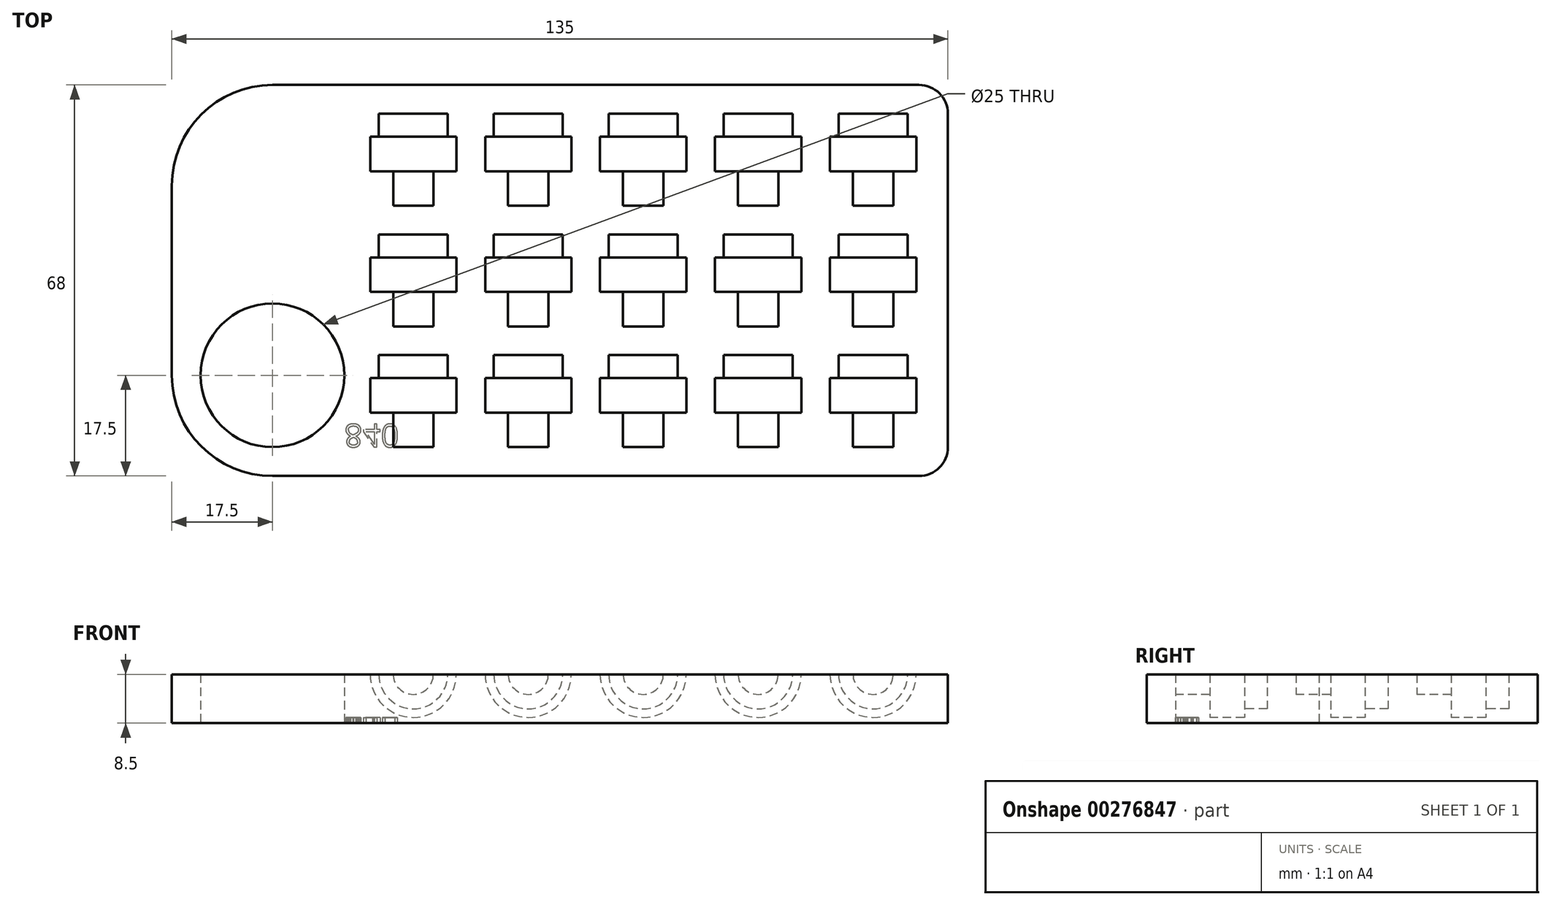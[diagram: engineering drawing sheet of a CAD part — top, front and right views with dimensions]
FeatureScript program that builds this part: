
annotation { "Feature Type Name" : "Feature", "Feature Type Description" : "" }
export const myFeature = defineFeature(function(context is Context, id is Id, definition is map)
    precondition{}
    {
        {
            var Q0;
            Q0=qCreatedBy(makeId("Top.planeOp"),FACE);
            var sketch = newSketch(context, id + "F0", { "sketchPlane" : qUnion([Q0])});
            skLineSegment(sketch, "E0.bottom", {"start": v(17.5, 0) * mm, "end": v(130, 0) * mm});
            skLineSegment(sketch, "E0.top", {"start": v(17.5, 68) * mm, "end": v(130, 68) * mm});
            skLineSegment(sketch, "E0.left", {"start": v(0, 17.5) * mm, "end": v(0, 50.5) * mm});
            skLineSegment(sketch, "E0.right", {"start": v(135, 5) * mm, "end": v(135, 63) * mm});
            skLineSegment(sketch, "E1.bottom", {"start": v(0, 0) * mm, "end": v(17.5, 0) * mm, "construction": true});
            skLineSegment(sketch, "E1.top", {"start": v(0, 17.5) * mm, "end": v(17.5, 17.5) * mm, "construction": true});
            skLineSegment(sketch, "E1.left", {"start": v(0, 0) * mm, "end": v(0, 17.5) * mm, "construction": true});
            skLineSegment(sketch, "E1.right", {"start": v(17.5, 0) * mm, "end": v(17.5, 17.5) * mm, "construction": true});
            skCircle(sketch, "E2", {"center": v(17.5, 17.5) * mm, "radius": 12.5 * mm});
            skPoint(sketch, "E3.visualSharp", {"position": v(0, 0) * mm});
            skArc(sketch, "E3.filletArc", {"start": v(0, 17.5) * mm, "mid": v(5.13, 5.13) * mm, "end": v(17.5, 0) * mm});
            skPoint(sketch, "E4.visualSharp", {"position": v(0, 68) * mm});
            skArc(sketch, "E4.filletArc", {"start": v(17.5, 68) * mm, "mid": v(5.13, 62.87) * mm, "end": v(0, 50.5) * mm});
            skPoint(sketch, "E5.visualSharp", {"position": v(135, 68) * mm});
            skArc(sketch, "E5.filletArc", {"start": v(135, 63) * mm, "mid": v(133.54, 66.54) * mm, "end": v(130, 68) * mm});
            skPoint(sketch, "E6.visualSharp", {"position": v(135, 0) * mm});
            skArc(sketch, "E6.filletArc", {"start": v(130, 0) * mm, "mid": v(133.54, 1.46) * mm, "end": v(135, 5) * mm});
            skSolve(sketch);
        }
        {
            var Q0;
            Q0=makeQuery(id+"F0.imprint","IMPRINT",FACE,{"disambiguationData":[TD([[makeQuery(id+"F0.imprint","IMPRINT",EDGE,{"derivedFrom":sQuery(id+"F0.wireOp",EDGE,"E0.bottom")}),1.0]])]});
            extrude(context, id + "F1", {"entities" : qUnion([Q0]), "depth" : 8.5 * mm});
        }
        {
            var Q0;
            Q0=makeQuery(id+"F1.opExtrude","CAP_FACE",FACE,{"disambiguationData":[OSD([sQuery(id+"F0.wireOp",EDGE,"E0.bottom"),sQuery(id+"F0.wireOp",EDGE,"E0.top"),sQuery(id+"F0.wireOp",EDGE,"E0.left"),sQuery(id+"F0.wireOp",EDGE,"E0.right"),sQuery(id+"F0.wireOp",EDGE,"E2"),sQuery(id+"F0.wireOp",EDGE,"E3.filletArc"),sQuery(id+"F0.wireOp",EDGE,"E4.filletArc"),sQuery(id+"F0.wireOp",EDGE,"E5.filletArc"),sQuery(id+"F0.wireOp",EDGE,"E6.filletArc")])],"isStart":false});
            var sketch = newSketch(context, id + "F2", { "sketchPlane" : qUnion([Q0])});
            skLineSegment(sketch, "E7.bottom", {"start": v(0, 0) * mm, "end": v(42, 0) * mm, "construction": true});
            skLineSegment(sketch, "E7.top", {"start": v(0, 21) * mm, "end": v(42, 21) * mm, "construction": true});
            skLineSegment(sketch, "E7.left", {"start": v(0, 0) * mm, "end": v(0, 21) * mm, "construction": true});
            skLineSegment(sketch, "E7.right", {"start": v(42, 0) * mm, "end": v(42, 21) * mm, "construction": true});
            skLineSegment(sketch, "E8.bottom", {"start": v(42, 21) * mm, "end": v(62, 21) * mm, "construction": true});
            skLineSegment(sketch, "E8.top", {"start": v(42, 42) * mm, "end": v(62, 42) * mm, "construction": true});
            skLineSegment(sketch, "E8.left", {"start": v(42, 21) * mm, "end": v(42, 42) * mm, "construction": true});
            skLineSegment(sketch, "E8.right", {"start": v(62, 21) * mm, "end": v(62, 42) * mm, "construction": true});
            skLineSegment(sketch, "E9.top", {"start": v(42, 63) * mm, "end": v(62, 63) * mm, "construction": true});
            skLineSegment(sketch, "E9.left", {"start": v(42, 42) * mm, "end": v(42, 63) * mm, "construction": true});
            skLineSegment(sketch, "E9.right", {"start": v(62, 42) * mm, "end": v(62, 63) * mm, "construction": true});
            skLineSegment(sketch, "E10.bottom", {"start": v(62, 21) * mm, "end": v(82, 21) * mm, "construction": true});
            skLineSegment(sketch, "E10.top", {"start": v(62, 42) * mm, "end": v(82, 42) * mm, "construction": true});
            skLineSegment(sketch, "E10.right", {"start": v(82, 21) * mm, "end": v(82, 42) * mm, "construction": true});
            skLineSegment(sketch, "E11.top", {"start": v(62, 63) * mm, "end": v(82, 63) * mm, "construction": true});
            skLineSegment(sketch, "E11.right", {"start": v(82, 42) * mm, "end": v(82, 63) * mm, "construction": true});
            skLineSegment(sketch, "E12.bottom", {"start": v(82, 21) * mm, "end": v(102, 21) * mm, "construction": true});
            skLineSegment(sketch, "E12.top", {"start": v(82, 42) * mm, "end": v(102, 42) * mm, "construction": true});
            skLineSegment(sketch, "E12.right", {"start": v(102, 21) * mm, "end": v(102, 42) * mm, "construction": true});
            skLineSegment(sketch, "E13.top", {"start": v(82, 63) * mm, "end": v(102, 63) * mm, "construction": true});
            skLineSegment(sketch, "E13.right", {"start": v(102, 42) * mm, "end": v(102, 63) * mm, "construction": true});
            skLineSegment(sketch, "E14.bottom", {"start": v(102, 21) * mm, "end": v(122, 21) * mm, "construction": true});
            skLineSegment(sketch, "E14.top", {"start": v(102, 42) * mm, "end": v(122, 42) * mm, "construction": true});
            skLineSegment(sketch, "E14.right", {"start": v(122, 21) * mm, "end": v(122, 42) * mm, "construction": true});
            skLineSegment(sketch, "E15.top", {"start": v(102, 63) * mm, "end": v(122, 63) * mm, "construction": true});
            skLineSegment(sketch, "E15.right", {"start": v(122, 42) * mm, "end": v(122, 63) * mm, "construction": true});
            skLineSegment(sketch, "E16.bottom", {"start": v(42, 63) * mm, "end": v(48, 63) * mm});
            skLineSegment(sketch, "E16.left", {"start": v(42, 63) * mm, "end": v(42, 59) * mm});
            skLineSegment(sketch, "E16.right", {"start": v(48, 63) * mm, "end": v(48, 59) * mm});
            skLineSegment(sketch, "E17.bottom", {"start": v(62, 63) * mm, "end": v(68, 63) * mm});
            skLineSegment(sketch, "E17.left", {"start": v(62, 63) * mm, "end": v(62, 59) * mm});
            skLineSegment(sketch, "E17.right", {"start": v(68, 63) * mm, "end": v(68, 59) * mm});
            skLineSegment(sketch, "E18.bottom", {"start": v(82, 63) * mm, "end": v(88, 63) * mm});
            skLineSegment(sketch, "E18.left", {"start": v(82, 63) * mm, "end": v(82, 59) * mm});
            skLineSegment(sketch, "E18.right", {"start": v(88, 63) * mm, "end": v(88, 59) * mm});
            skLineSegment(sketch, "E19.bottom", {"start": v(102, 63) * mm, "end": v(108, 63) * mm});
            skLineSegment(sketch, "E19.left", {"start": v(102, 63) * mm, "end": v(102, 59) * mm});
            skLineSegment(sketch, "E19.right", {"start": v(108, 63) * mm, "end": v(108, 59) * mm});
            skLineSegment(sketch, "E20.bottom", {"start": v(42, 42) * mm, "end": v(48, 42) * mm});
            skLineSegment(sketch, "E20.left", {"start": v(42, 42) * mm, "end": v(42, 38) * mm});
            skLineSegment(sketch, "E20.right", {"start": v(48, 42) * mm, "end": v(48, 38) * mm});
            skLineSegment(sketch, "E21.bottom", {"start": v(62, 42) * mm, "end": v(68, 42) * mm});
            skLineSegment(sketch, "E21.left", {"start": v(62, 42) * mm, "end": v(62, 38) * mm});
            skLineSegment(sketch, "E21.right", {"start": v(68, 42) * mm, "end": v(68, 38) * mm});
            skLineSegment(sketch, "E22.bottom", {"start": v(82, 42) * mm, "end": v(88, 42) * mm});
            skLineSegment(sketch, "E22.left", {"start": v(82, 42) * mm, "end": v(82, 38) * mm});
            skLineSegment(sketch, "E22.right", {"start": v(88, 42) * mm, "end": v(88, 38) * mm});
            skLineSegment(sketch, "E23.bottom", {"start": v(102, 42) * mm, "end": v(108, 42) * mm});
            skLineSegment(sketch, "E23.left", {"start": v(102, 42) * mm, "end": v(102, 38) * mm});
            skLineSegment(sketch, "E23.right", {"start": v(108, 42) * mm, "end": v(108, 38) * mm});
            skLineSegment(sketch, "E24.bottom", {"start": v(42, 21) * mm, "end": v(48, 21) * mm});
            skLineSegment(sketch, "E24.left", {"start": v(42, 21) * mm, "end": v(42, 17) * mm});
            skLineSegment(sketch, "E24.right", {"start": v(48, 21) * mm, "end": v(48, 17) * mm});
            skPoint(sketch, "E25.oppositeSnap0", {"position": v(68, 40) * mm});
            skLineSegment(sketch, "E25.bottom", {"start": v(62, 21) * mm, "end": v(68, 21) * mm});
            skLineSegment(sketch, "E25.left", {"start": v(62, 21) * mm, "end": v(62, 17) * mm});
            skLineSegment(sketch, "E25.right", {"start": v(68, 21) * mm, "end": v(68, 17) * mm});
            skLineSegment(sketch, "E26.bottom", {"start": v(82, 21) * mm, "end": v(88, 21) * mm});
            skLineSegment(sketch, "E26.left", {"start": v(82, 21) * mm, "end": v(82, 17) * mm});
            skLineSegment(sketch, "E26.right", {"start": v(88, 21) * mm, "end": v(88, 17) * mm});
            skLineSegment(sketch, "E27.bottom", {"start": v(102, 21) * mm, "end": v(108, 21) * mm});
            skLineSegment(sketch, "E27.left", {"start": v(102, 21) * mm, "end": v(102, 17) * mm});
            skLineSegment(sketch, "E27.right", {"start": v(108, 21) * mm, "end": v(108, 17) * mm});
            skLineSegment(sketch, "E28.bottom", {"start": v(48, 59) * mm, "end": v(49.5, 59) * mm});
            skLineSegment(sketch, "E28.top", {"start": v(45.5, 53) * mm, "end": v(49.5, 53) * mm});
            skLineSegment(sketch, "E28.left", {"start": v(42, 59) * mm, "end": v(42, 53) * mm});
            skLineSegment(sketch, "E28.right", {"start": v(49.5, 59) * mm, "end": v(49.5, 53) * mm});
            skLineSegment(sketch, "E29.bottom", {"start": v(68, 59) * mm, "end": v(69.5, 59) * mm});
            skLineSegment(sketch, "E29.top", {"start": v(65.5, 53) * mm, "end": v(69.5, 53) * mm});
            skLineSegment(sketch, "E29.left", {"start": v(62, 59) * mm, "end": v(62, 53) * mm});
            skLineSegment(sketch, "E29.right", {"start": v(69.5, 59) * mm, "end": v(69.5, 53) * mm});
            skLineSegment(sketch, "E30.bottom", {"start": v(88, 59) * mm, "end": v(89.5, 59) * mm});
            skLineSegment(sketch, "E30.top", {"start": v(85.5, 53) * mm, "end": v(89.5, 53) * mm});
            skLineSegment(sketch, "E30.left", {"start": v(82, 59) * mm, "end": v(82, 53) * mm});
            skLineSegment(sketch, "E30.right", {"start": v(89.5, 59) * mm, "end": v(89.5, 53) * mm});
            skLineSegment(sketch, "E31.bottom", {"start": v(108, 59) * mm, "end": v(109.5, 59) * mm});
            skLineSegment(sketch, "E31.top", {"start": v(105.5, 53) * mm, "end": v(109.5, 53) * mm});
            skLineSegment(sketch, "E31.left", {"start": v(102, 59) * mm, "end": v(102, 53) * mm});
            skLineSegment(sketch, "E31.right", {"start": v(109.5, 59) * mm, "end": v(109.5, 53) * mm});
            skLineSegment(sketch, "E32.bottom", {"start": v(48, 38) * mm, "end": v(49.5, 38) * mm});
            skLineSegment(sketch, "E32.top", {"start": v(45.5, 32) * mm, "end": v(49.5, 32) * mm});
            skLineSegment(sketch, "E32.left", {"start": v(42, 38) * mm, "end": v(42, 32) * mm});
            skLineSegment(sketch, "E32.right", {"start": v(49.5, 38) * mm, "end": v(49.5, 32) * mm});
            skLineSegment(sketch, "E33.bottom", {"start": v(68, 38) * mm, "end": v(69.5, 38) * mm});
            skLineSegment(sketch, "E33.top", {"start": v(65.5, 32) * mm, "end": v(69.5, 32) * mm});
            skLineSegment(sketch, "E33.left", {"start": v(62, 38) * mm, "end": v(62, 32) * mm});
            skLineSegment(sketch, "E33.right", {"start": v(69.5, 38) * mm, "end": v(69.5, 32) * mm});
            skLineSegment(sketch, "E34.bottom", {"start": v(88, 38) * mm, "end": v(89.5, 38) * mm});
            skLineSegment(sketch, "E34.top", {"start": v(85.5, 32) * mm, "end": v(89.5, 32) * mm});
            skLineSegment(sketch, "E34.left", {"start": v(82, 38) * mm, "end": v(82, 32) * mm});
            skLineSegment(sketch, "E34.right", {"start": v(89.5, 38) * mm, "end": v(89.5, 32) * mm});
            skLineSegment(sketch, "E35.bottom", {"start": v(108, 38) * mm, "end": v(109.5, 38) * mm});
            skLineSegment(sketch, "E35.top", {"start": v(105.5, 32) * mm, "end": v(109.5, 32) * mm});
            skLineSegment(sketch, "E35.left", {"start": v(102, 38) * mm, "end": v(102, 32) * mm});
            skLineSegment(sketch, "E35.right", {"start": v(109.5, 38) * mm, "end": v(109.5, 32) * mm});
            skLineSegment(sketch, "E36.bottom", {"start": v(48, 17) * mm, "end": v(49.5, 17) * mm});
            skLineSegment(sketch, "E36.top", {"start": v(45.5, 11) * mm, "end": v(49.5, 11) * mm});
            skLineSegment(sketch, "E36.left", {"start": v(42, 17) * mm, "end": v(42, 11) * mm});
            skLineSegment(sketch, "E36.right", {"start": v(49.5, 17) * mm, "end": v(49.5, 11) * mm});
            skLineSegment(sketch, "E37.bottom", {"start": v(68, 17) * mm, "end": v(69.5, 17) * mm});
            skLineSegment(sketch, "E37.top", {"start": v(65.5, 11) * mm, "end": v(69.5, 11) * mm});
            skLineSegment(sketch, "E37.left", {"start": v(62, 17) * mm, "end": v(62, 11) * mm});
            skLineSegment(sketch, "E37.right", {"start": v(69.5, 17) * mm, "end": v(69.5, 11) * mm});
            skLineSegment(sketch, "E38.bottom", {"start": v(88, 17) * mm, "end": v(89.5, 17) * mm});
            skLineSegment(sketch, "E38.top", {"start": v(85.5, 11) * mm, "end": v(89.5, 11) * mm});
            skLineSegment(sketch, "E38.left", {"start": v(82, 17) * mm, "end": v(82, 11) * mm});
            skLineSegment(sketch, "E38.right", {"start": v(89.5, 17) * mm, "end": v(89.5, 11) * mm});
            skLineSegment(sketch, "E39.bottom", {"start": v(108, 17) * mm, "end": v(109.5, 17) * mm});
            skLineSegment(sketch, "E39.top", {"start": v(105.5, 11) * mm, "end": v(109.5, 11) * mm});
            skLineSegment(sketch, "E39.left", {"start": v(102, 17) * mm, "end": v(102, 11) * mm});
            skLineSegment(sketch, "E39.right", {"start": v(109.5, 17) * mm, "end": v(109.5, 11) * mm});
            skLineSegment(sketch, "E40.top", {"start": v(42, 47) * mm, "end": v(45.5, 47) * mm});
            skLineSegment(sketch, "E40.left", {"start": v(42, 53) * mm, "end": v(42, 47) * mm});
            skLineSegment(sketch, "E40.right", {"start": v(45.5, 53) * mm, "end": v(45.5, 47) * mm});
            skLineSegment(sketch, "E41.top", {"start": v(62, 47) * mm, "end": v(65.5, 47) * mm});
            skLineSegment(sketch, "E41.left", {"start": v(62, 53) * mm, "end": v(62, 47) * mm});
            skLineSegment(sketch, "E41.right", {"start": v(65.5, 53) * mm, "end": v(65.5, 47) * mm});
            skLineSegment(sketch, "E42.top", {"start": v(82, 47) * mm, "end": v(85.5, 47) * mm});
            skLineSegment(sketch, "E42.left", {"start": v(82, 53) * mm, "end": v(82, 47) * mm});
            skLineSegment(sketch, "E42.right", {"start": v(85.5, 53) * mm, "end": v(85.5, 47) * mm});
            skLineSegment(sketch, "E43.top", {"start": v(102, 47) * mm, "end": v(105.5, 47) * mm});
            skLineSegment(sketch, "E43.left", {"start": v(102, 53) * mm, "end": v(102, 47) * mm});
            skLineSegment(sketch, "E43.right", {"start": v(105.5, 53) * mm, "end": v(105.5, 47) * mm});
            skLineSegment(sketch, "E44.top", {"start": v(42, 26) * mm, "end": v(45.5, 26) * mm});
            skLineSegment(sketch, "E44.left", {"start": v(42, 32) * mm, "end": v(42, 26) * mm});
            skLineSegment(sketch, "E44.right", {"start": v(45.5, 32) * mm, "end": v(45.5, 26) * mm});
            skLineSegment(sketch, "E45.top", {"start": v(62, 26) * mm, "end": v(65.5, 26) * mm});
            skLineSegment(sketch, "E45.left", {"start": v(62, 32) * mm, "end": v(62, 26) * mm});
            skLineSegment(sketch, "E45.right", {"start": v(65.5, 32) * mm, "end": v(65.5, 26) * mm});
            skLineSegment(sketch, "E46.top", {"start": v(82, 26) * mm, "end": v(85.5, 26) * mm});
            skLineSegment(sketch, "E46.left", {"start": v(82, 32) * mm, "end": v(82, 26) * mm});
            skLineSegment(sketch, "E46.right", {"start": v(85.5, 32) * mm, "end": v(85.5, 26) * mm});
            skLineSegment(sketch, "E47.top", {"start": v(102, 26) * mm, "end": v(105.5, 26) * mm});
            skLineSegment(sketch, "E47.left", {"start": v(102, 32) * mm, "end": v(102, 26) * mm});
            skLineSegment(sketch, "E47.right", {"start": v(105.5, 32) * mm, "end": v(105.5, 26) * mm});
            skLineSegment(sketch, "E48.top", {"start": v(42, 5) * mm, "end": v(45.5, 5) * mm});
            skLineSegment(sketch, "E48.left", {"start": v(42, 11) * mm, "end": v(42, 5) * mm});
            skLineSegment(sketch, "E48.right", {"start": v(45.5, 11) * mm, "end": v(45.5, 5) * mm});
            skPoint(sketch, "E49.oppositeSnap0", {"position": v(43.75, 5) * mm});
            skLineSegment(sketch, "E49.top", {"start": v(62, 5) * mm, "end": v(65.5, 5) * mm});
            skLineSegment(sketch, "E49.left", {"start": v(62, 11) * mm, "end": v(62, 5) * mm});
            skLineSegment(sketch, "E49.right", {"start": v(65.5, 11) * mm, "end": v(65.5, 5) * mm});
            skLineSegment(sketch, "E50.top", {"start": v(82, 5) * mm, "end": v(85.5, 5) * mm});
            skLineSegment(sketch, "E50.left", {"start": v(82, 11) * mm, "end": v(82, 5) * mm});
            skLineSegment(sketch, "E50.right", {"start": v(85.5, 11) * mm, "end": v(85.5, 5) * mm});
            skLineSegment(sketch, "E51.top", {"start": v(102, 5) * mm, "end": v(105.5, 5) * mm});
            skLineSegment(sketch, "E51.left", {"start": v(102, 11) * mm, "end": v(102, 5) * mm});
            skLineSegment(sketch, "E51.right", {"start": v(105.5, 11) * mm, "end": v(105.5, 5) * mm});
            skLineSegment(sketch, "E52.bottom", {"start": v(122, 63) * mm, "end": v(128, 63) * mm});
            skLineSegment(sketch, "E52.left", {"start": v(122, 63) * mm, "end": v(122, 59) * mm});
            skLineSegment(sketch, "E52.right", {"start": v(128, 63) * mm, "end": v(128, 59) * mm});
            skLineSegment(sketch, "E53.bottom", {"start": v(122, 42) * mm, "end": v(128, 42) * mm});
            skLineSegment(sketch, "E53.left", {"start": v(122, 42) * mm, "end": v(122, 38) * mm});
            skLineSegment(sketch, "E53.right", {"start": v(128, 42) * mm, "end": v(128, 38) * mm});
            skLineSegment(sketch, "E54.bottom", {"start": v(122, 21) * mm, "end": v(128, 21) * mm});
            skLineSegment(sketch, "E54.left", {"start": v(122, 21) * mm, "end": v(122, 17) * mm});
            skLineSegment(sketch, "E54.right", {"start": v(128, 21) * mm, "end": v(128, 17) * mm});
            skLineSegment(sketch, "E55.bottom", {"start": v(128, 59) * mm, "end": v(129.5, 59) * mm});
            skLineSegment(sketch, "E55.top", {"start": v(125.5, 53) * mm, "end": v(129.5, 53) * mm});
            skLineSegment(sketch, "E55.left", {"start": v(122, 59) * mm, "end": v(122, 53) * mm});
            skLineSegment(sketch, "E55.right", {"start": v(129.5, 59) * mm, "end": v(129.5, 53) * mm});
            skLineSegment(sketch, "E56.bottom", {"start": v(128, 38) * mm, "end": v(129.5, 38) * mm});
            skLineSegment(sketch, "E56.top", {"start": v(125.5, 32) * mm, "end": v(129.5, 32) * mm});
            skLineSegment(sketch, "E56.left", {"start": v(122, 38) * mm, "end": v(122, 32) * mm});
            skLineSegment(sketch, "E56.right", {"start": v(129.5, 38) * mm, "end": v(129.5, 32) * mm});
            skLineSegment(sketch, "E57.bottom", {"start": v(128, 17) * mm, "end": v(129.5, 17) * mm});
            skLineSegment(sketch, "E57.top", {"start": v(125.5, 11) * mm, "end": v(129.5, 11) * mm});
            skLineSegment(sketch, "E57.left", {"start": v(122, 17) * mm, "end": v(122, 11) * mm});
            skLineSegment(sketch, "E57.right", {"start": v(129.5, 17) * mm, "end": v(129.5, 11) * mm});
            skLineSegment(sketch, "E58.top", {"start": v(122, 47) * mm, "end": v(125.5, 47) * mm});
            skLineSegment(sketch, "E58.left", {"start": v(122, 53) * mm, "end": v(122, 47) * mm});
            skLineSegment(sketch, "E58.right", {"start": v(125.5, 53) * mm, "end": v(125.5, 47) * mm});
            skLineSegment(sketch, "E59.top", {"start": v(122, 26) * mm, "end": v(125.5, 26) * mm});
            skLineSegment(sketch, "E59.left", {"start": v(122, 32) * mm, "end": v(122, 26) * mm});
            skLineSegment(sketch, "E59.right", {"start": v(125.5, 32) * mm, "end": v(125.5, 26) * mm});
            skLineSegment(sketch, "E60.top", {"start": v(122, 5) * mm, "end": v(125.5, 5) * mm});
            skLineSegment(sketch, "E60.left", {"start": v(122, 11) * mm, "end": v(122, 5) * mm});
            skLineSegment(sketch, "E60.right", {"start": v(125.5, 11) * mm, "end": v(125.5, 5) * mm});
            skSolve(sketch);
        }
        {
            var Q0;
            Q0=makeQuery(id+"F2.imprint","IMPRINT",FACE,{"disambiguationData":[TD([[makeQuery(id+"F2.imprint","IMPRINT",EDGE,{"derivedFrom":sQuery(id+"F2.wireOp",EDGE,"E24.bottom")}),-1.0]])]});
            var Q1;
            Q1=makeQuery(id+"F2.imprint","IMPRINT",FACE,{"disambiguationData":[TD([[makeQuery(id+"F2.imprint","IMPRINT",EDGE,{"derivedFrom":sQuery(id+"F2.wireOp",EDGE,"E20.bottom")}),-1.0]])]});
            var Q2;
            Q2=makeQuery(id+"F2.imprint","IMPRINT",FACE,{"disambiguationData":[TD([[makeQuery(id+"F2.imprint","IMPRINT",EDGE,{"derivedFrom":sQuery(id+"F2.wireOp",EDGE,"E16.bottom")}),-1.0]])]});
            var Q3;
            Q3=sQuery(id+"F2.wireOp",EDGE,"E40.left");
            revolve(context, id + "F3", {"operationType" : NewBodyOperationType.REMOVE, "entities" : qUnion([Q0, Q1, Q2]), "axis" : qUnion([Q3]), "revolveType" : RevolveType.FULL, "oppositeDirection" : true});
        }
        {
            var Q0;
            Q0=makeQuery(id+"F2.imprint","IMPRINT",FACE,{"disambiguationData":[TD([[makeQuery(id+"F2.imprint","IMPRINT",EDGE,{"derivedFrom":sQuery(id+"F2.wireOp",EDGE,"E25.bottom")}),-1.0]])]});
            var Q1;
            Q1=makeQuery(id+"F2.imprint","IMPRINT",FACE,{"disambiguationData":[TD([[makeQuery(id+"F2.imprint","IMPRINT",EDGE,{"derivedFrom":sQuery(id+"F2.wireOp",EDGE,"E21.bottom")}),-1.0]])]});
            var Q2;
            Q2=makeQuery(id+"F2.imprint","IMPRINT",FACE,{"disambiguationData":[TD([[makeQuery(id+"F2.imprint","IMPRINT",EDGE,{"derivedFrom":sQuery(id+"F2.wireOp",EDGE,"E17.bottom")}),-1.0]])]});
            var Q3;
            Q3=sQuery(id+"F2.wireOp",EDGE,"E29.left");
            revolve(context, id + "F4", {"operationType" : NewBodyOperationType.REMOVE, "entities" : qUnion([Q0, Q1, Q2]), "axis" : qUnion([Q3]), "revolveType" : RevolveType.FULL, "oppositeDirection" : true});
        }
        {
            var Q0;
            Q0=makeQuery(id+"F2.imprint","IMPRINT",FACE,{"disambiguationData":[TD([[makeQuery(id+"F2.imprint","IMPRINT",EDGE,{"derivedFrom":sQuery(id+"F2.wireOp",EDGE,"E26.bottom")}),-1.0]])]});
            var Q1;
            Q1=makeQuery(id+"F2.imprint","IMPRINT",FACE,{"disambiguationData":[TD([[makeQuery(id+"F2.imprint","IMPRINT",EDGE,{"derivedFrom":sQuery(id+"F2.wireOp",EDGE,"E22.bottom")}),-1.0]])]});
            var Q2;
            Q2=makeQuery(id+"F2.imprint","IMPRINT",FACE,{"disambiguationData":[TD([[makeQuery(id+"F2.imprint","IMPRINT",EDGE,{"derivedFrom":sQuery(id+"F2.wireOp",EDGE,"E18.bottom")}),-1.0]])]});
            var Q3;
            Q3=sQuery(id+"F2.wireOp",EDGE,"E30.left");
            revolve(context, id + "F5", {"operationType" : NewBodyOperationType.REMOVE, "entities" : qUnion([Q0, Q1, Q2]), "axis" : qUnion([Q3]), "revolveType" : RevolveType.FULL, "oppositeDirection" : true});
        }
        {
            var Q0;
            Q0=makeQuery(id+"F2.imprint","IMPRINT",FACE,{"disambiguationData":[TD([[makeQuery(id+"F2.imprint","IMPRINT",EDGE,{"derivedFrom":sQuery(id+"F2.wireOp",EDGE,"E27.bottom")}),-1.0]])]});
            var Q1;
            Q1=makeQuery(id+"F2.imprint","IMPRINT",FACE,{"disambiguationData":[TD([[makeQuery(id+"F2.imprint","IMPRINT",EDGE,{"derivedFrom":sQuery(id+"F2.wireOp",EDGE,"E23.bottom")}),-1.0]])]});
            var Q2;
            Q2=makeQuery(id+"F2.imprint","IMPRINT",FACE,{"disambiguationData":[TD([[makeQuery(id+"F2.imprint","IMPRINT",EDGE,{"derivedFrom":sQuery(id+"F2.wireOp",EDGE,"E19.bottom")}),-1.0]])]});
            var Q3;
            Q3=sQuery(id+"F2.wireOp",EDGE,"E31.left");
            revolve(context, id + "F6", {"operationType" : NewBodyOperationType.REMOVE, "entities" : qUnion([Q0, Q1, Q2]), "axis" : qUnion([Q3]), "revolveType" : RevolveType.FULL, "oppositeDirection" : true});
        }
        {
            var Q0;
            Q0=makeQuery(id+"F2.imprint","IMPRINT",FACE,{"disambiguationData":[TD([[makeQuery(id+"F2.imprint","IMPRINT",EDGE,{"derivedFrom":sQuery(id+"F2.wireOp",EDGE,"E54.bottom")}),-1.0]])]});
            var Q1;
            Q1=makeQuery(id+"F2.imprint","IMPRINT",FACE,{"disambiguationData":[TD([[makeQuery(id+"F2.imprint","IMPRINT",EDGE,{"derivedFrom":sQuery(id+"F2.wireOp",EDGE,"E53.bottom")}),-1.0]])]});
            var Q2;
            Q2=makeQuery(id+"F2.imprint","IMPRINT",FACE,{"disambiguationData":[TD([[makeQuery(id+"F2.imprint","IMPRINT",EDGE,{"derivedFrom":sQuery(id+"F2.wireOp",EDGE,"E52.bottom")}),-1.0]])]});
            var Q3;
            Q3=sQuery(id+"F2.wireOp",EDGE,"E55.left");
            revolve(context, id + "F7", {"operationType" : NewBodyOperationType.REMOVE, "entities" : qUnion([Q0, Q1, Q2]), "axis" : qUnion([Q3]), "revolveType" : RevolveType.FULL, "oppositeDirection" : true});
        }
        {
            var Q0;
            Q0=makeQuery(id+"F1.opExtrude","CAP_FACE",FACE,{"disambiguationData":[OSD([sQuery(id+"F0.wireOp",EDGE,"E0.bottom"),sQuery(id+"F0.wireOp",EDGE,"E0.top"),sQuery(id+"F0.wireOp",EDGE,"E0.left"),sQuery(id+"F0.wireOp",EDGE,"E0.right"),sQuery(id+"F0.wireOp",EDGE,"E2"),sQuery(id+"F0.wireOp",EDGE,"E3.filletArc"),sQuery(id+"F0.wireOp",EDGE,"E4.filletArc"),sQuery(id+"F0.wireOp",EDGE,"E5.filletArc"),sQuery(id+"F0.wireOp",EDGE,"E6.filletArc")])],"isStart":true});
            var sketch = newSketch(context, id + "F8", { "sketchPlane" : qUnion([Q0])});
            skLineSegment(sketch, "E61.bottom", {"start": v(0, 0) * mm, "end": v(30, 0) * mm, "construction": true});
            skLineSegment(sketch, "E61.top", {"start": v(0, -5) * mm, "end": v(30, -5) * mm, "construction": true});
            skLineSegment(sketch, "E61.left", {"start": v(0, 0) * mm, "end": v(0, -5) * mm, "construction": true});
            skLineSegment(sketch, "E61.right", {"start": v(30, 0) * mm, "end": v(30, -5) * mm, "construction": true});
            skText(sketch, "E62", { "text": "840", "fontName": "OpenSans-Regular.ttf"});
            const initialGuessF8  = {"E62": [0.03, -0.009, 1, 0, 0.004]};
            skSetInitialGuess(sketch, initialGuessF8);
            skSolve(sketch);
        }
        {
            var Q0;
            Q0 = qSketchRegion(id + "F8", true);
            extrude(context, id + "F9", {"entities" : qUnion([Q0]), "operationType" : NewBodyOperationType.REMOVE, "oppositeDirection" : true, "depth" : 1 * mm});
        }
    });
